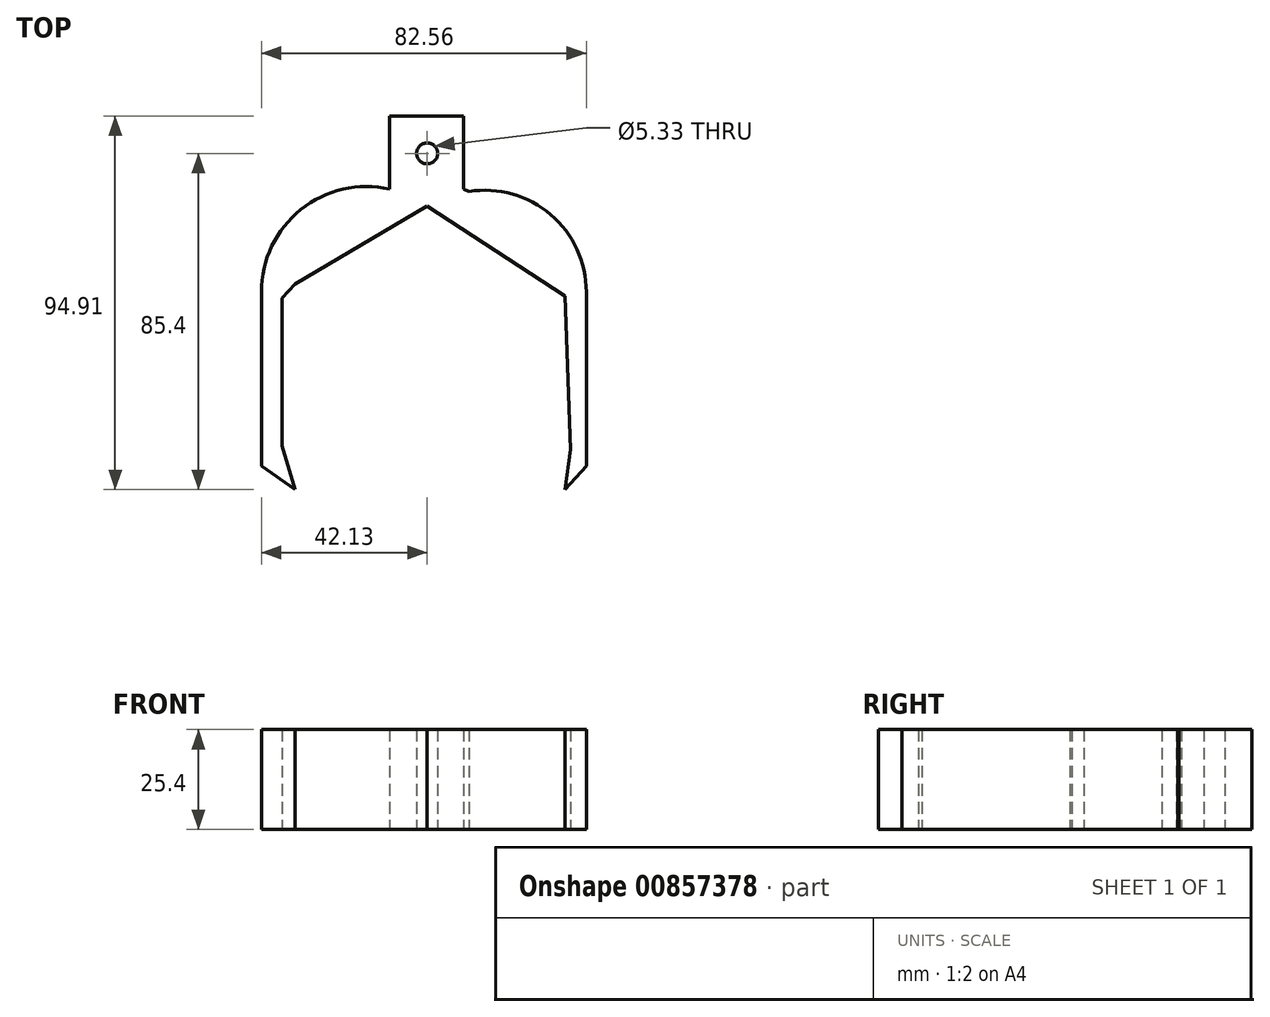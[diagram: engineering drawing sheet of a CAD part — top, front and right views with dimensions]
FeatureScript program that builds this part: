
annotation { "Feature Type Name" : "Feature", "Feature Type Description" : "" }
export const myFeature = defineFeature(function(context is Context, id is Id, definition is map)
    precondition{}
    {
        {
            var Q0;
            Q0=qCreatedBy(makeId("Top.planeOp"),FACE);
            var sketch = newSketch(context, id + "F0", { "sketchPlane" : qUnion([Q0])});
            skLineSegment(sketch, "E0", {"start": v(-42.13, 28.8) * mm, "end": v(-42.13, -15.46) * mm});
            skLineSegment(sketch, "E1", {"start": v(40.43, 28.8) * mm, "end": v(40.43, -15.46) * mm});
            skLineSegment(sketch, "E2", {"start": v(40.43, -15.46) * mm, "end": v(35.04, -21.42) * mm});
            skLineSegment(sketch, "E3", {"start": v(35.04, -21.42) * mm, "end": v(36.46, -11.2) * mm});
            skLineSegment(sketch, "E4", {"start": v(36.46, -11.2) * mm, "end": v(35.04, 27.7) * mm});
            skLineSegment(sketch, "E5", {"start": v(35.04, 27.7) * mm, "end": v(0, 50.56) * mm});
            skLineSegment(sketch, "E6", {"start": v(0, 50.56) * mm, "end": v(-33.59, 30.83) * mm});
            skLineSegment(sketch, "E7", {"start": v(-33.59, 30.83) * mm, "end": v(-36.88, 27.19) * mm});
            skLineSegment(sketch, "E8", {"start": v(-36.88, 27.19) * mm, "end": v(-36.88, -10.33) * mm});
            skLineSegment(sketch, "E9", {"start": v(-36.88, -10.33) * mm, "end": v(-33.59, -21.42) * mm});
            skLineSegment(sketch, "E10", {"start": v(-33.59, -21.42) * mm, "end": v(-42.13, -15.46) * mm});
            skArc(sketch, "E11", {"start": v(-9.54, 54.89) * mm, "mid": v(-32.1, 49.67) * mm, "end": v(-42.13, 28.8) * mm});
            skArc(sketch, "E12", {"start": v(40.43, 28.8) * mm, "mid": v(31.4, 48.42) * mm, "end": v(10.6, 54.3) * mm});
            skLineSegment(sketch, "E13", {"start": v(-9.54, 54.89) * mm, "end": v(-9.54, 73.5) * mm});
            skLineSegment(sketch, "E14", {"start": v(-9.54, 73.5) * mm, "end": v(9.18, 73.5) * mm});
            skLineSegment(sketch, "E15", {"start": v(9.18, 73.5) * mm, "end": v(9.18, 54.89) * mm});
            skLineSegment(sketch, "E16", {"start": v(9.18, 54.89) * mm, "end": v(10.6, 54.3) * mm});
            skCircle(sketch, "E17", {"center": v(0, 63.98) * mm, "radius": 2.66 * mm});
            skSolve(sketch);
        }
        {
            var Q0;
            Q0=qSketchRegion(id+"F0",true);
            extrude(context, id + "F1", {"entities" : qUnion([Q0]), "depth" : 25.4 * mm, "offsetDistance" : 25.4 * mm});
        }
        {
            var Q0;
            Q0=qSketchRegion(id+"F0",true);
            extrude(context, id + "F2", {"entities" : qUnion([Q0]), "operationType" : NewBodyOperationType.ADD, "depth" : 25.4 * mm, "offsetDistance" : 25.4 * mm});
        }
    });
